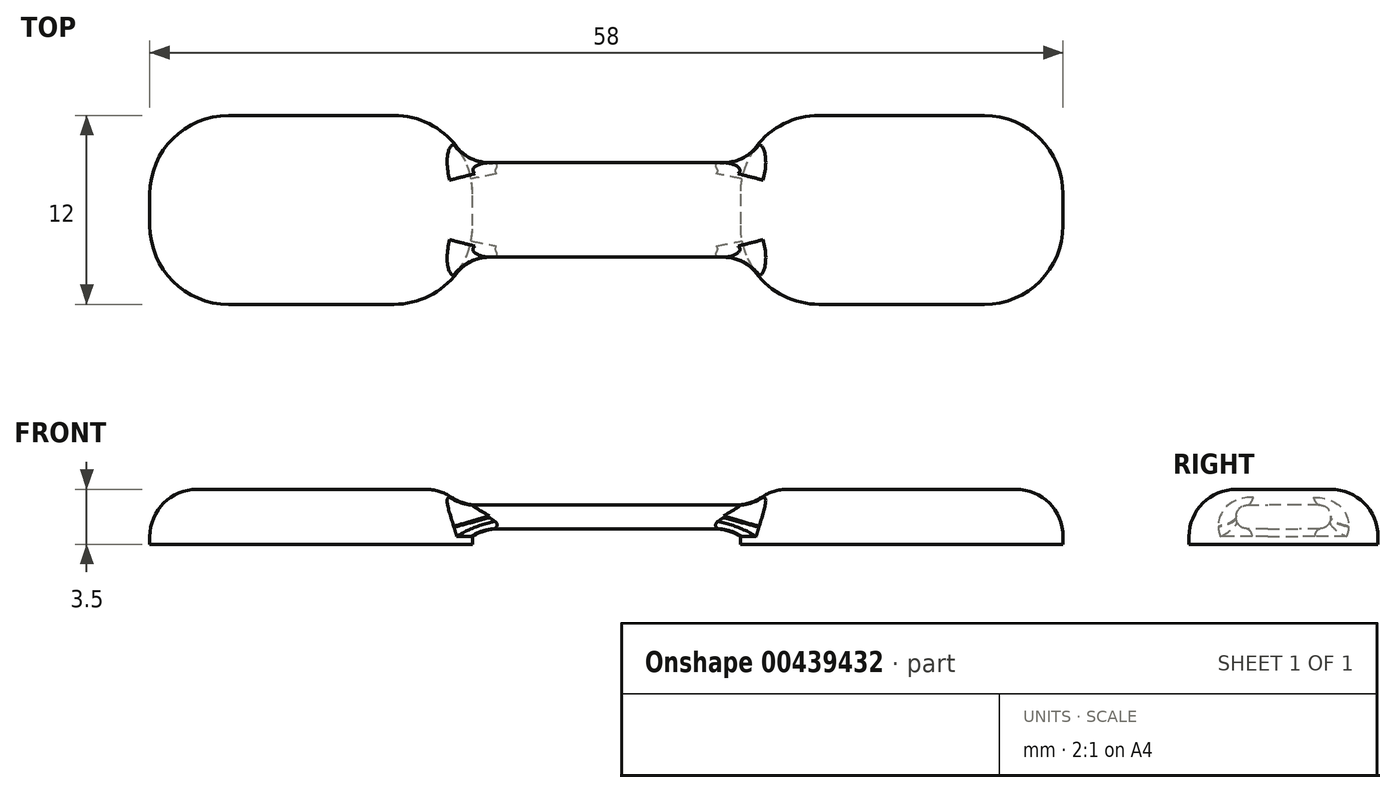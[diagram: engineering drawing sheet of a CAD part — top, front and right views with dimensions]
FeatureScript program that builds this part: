
annotation { "Feature Type Name" : "Feature", "Feature Type Description" : "" }
export const myFeature = defineFeature(function(context is Context, id is Id, definition is map)
    precondition{}
    {
        {
            var Q0;
            Q0=qCreatedBy(makeId("Top.planeOp"),FACE);
            var sketch = newSketch(context, id + "F0", { "sketchPlane" : qUnion([Q0])});
            skLineSegment(sketch, "E0.bottom", {"start": v(-29, 6) * mm, "end": v(29, 6) * mm});
            skLineSegment(sketch, "E0.top", {"start": v(-29, -6) * mm, "end": v(29, -6) * mm});
            skLineSegment(sketch, "E0.left", {"start": v(-29, 6) * mm, "end": v(-29, -6) * mm});
            skLineSegment(sketch, "E0.right", {"start": v(29, 6) * mm, "end": v(29, -6) * mm});
            skPoint(sketch, "E0.middle", {"position": v(0, 0) * mm});
            skSolve(sketch);
        }
        {
            var Q0;
            Q0=qSketchRegion(id+"F0",true);
            extrude(context, id + "F1", {"entities" : qUnion([Q0]), "depth" : 3.5 * mm});
        }
        {
            var Q0;
            Q0=qCreatedBy(makeId("Right.planeOp"),FACE);
            var sketch = newSketch(context, id + "F2", { "sketchPlane" : qUnion([Q0])});
            skLineSegment(sketch, "E1.bottom", {"start": v(3, 1) * mm, "end": v(-3, 1) * mm});
            skLineSegment(sketch, "E1.top", {"start": v(3, 2.5) * mm, "end": v(-3, 2.5) * mm});
            skLineSegment(sketch, "E1.left", {"start": v(3, 1) * mm, "end": v(3, 2.5) * mm});
            skLineSegment(sketch, "E1.right", {"start": v(-3, 1) * mm, "end": v(-3, 2.5) * mm});
            skPoint(sketch, "E1.middle", {"position": v(0, 1.75) * mm});
            skLineSegment(sketch, "E2", {"start": v(0, 1.75) * mm, "end": v(0, 0) * mm, "construction": true});
            skLineSegment(sketch, "E3.bottom", {"start": v(7, -0.75) * mm, "end": v(-7, -0.75) * mm});
            skLineSegment(sketch, "E3.top", {"start": v(7, 4.25) * mm, "end": v(-7, 4.25) * mm});
            skLineSegment(sketch, "E3.left", {"start": v(7, -0.75) * mm, "end": v(7, 4.25) * mm});
            skLineSegment(sketch, "E3.right", {"start": v(-7, -0.75) * mm, "end": v(-7, 4.25) * mm});
            skSolve(sketch);
        }
        {
            var Q0;
            Q0=qSketchRegion(id+"F2",true);
            extrude(context, id + "F3", {"entities" : qUnion([Q0]), "operationType" : NewBodyOperationType.REMOVE, "endBound" : BoundingType.SYMMETRIC, "oppositeDirection" : true, "depth" : 17 * mm});
        }
        {
            var Q0;
            Q0=makeQuery(id+"F1.opExtrude","SWEPT_EDGE",EDGE,{"disambiguationData":[OSD([sQuery(id+"F0.wireOp",EDGE,"E0.top"),sQuery(id+"F0.wireOp",EDGE,"E0.right")])]});
            var Q1;
            Q1=makeQuery(id+"F1.opExtrude","SWEPT_EDGE",EDGE,{"disambiguationData":[OSD([sQuery(id+"F0.wireOp",EDGE,"E0.bottom"),sQuery(id+"F0.wireOp",EDGE,"E0.right")])]});
            var Q2;
            Q2=makeQuery(id+"F1.opExtrude","SWEPT_EDGE",EDGE,{"disambiguationData":[OSD([sQuery(id+"F0.wireOp",EDGE,"E0.top"),sQuery(id+"F0.wireOp",EDGE,"E0.left")])]});
            var Q3;
            Q3=makeQuery(id+"F1.opExtrude","SWEPT_EDGE",EDGE,{"disambiguationData":[OSD([sQuery(id+"F0.wireOp",EDGE,"E0.bottom"),sQuery(id+"F0.wireOp",EDGE,"E0.left")])]});
            var Q4;
            Q4=makeQuery(id+"F3.boolean.opBoolean","INTERSECT",EDGE,{"derivedFrom":[makeQuery(id+"F1.opExtrude","SWEPT_FACE",FACE,{"disambiguationData":[OSD([sQuery(id+"F0.wireOp",EDGE,"E0.top")])]}),makeQuery(id+"F3.opExtrude","CAP_FACE",FACE,{"disambiguationData":[OSD([sQuery(id+"F2.wireOp",EDGE,"E1.bottom"),sQuery(id+"F2.wireOp",EDGE,"E1.top"),sQuery(id+"F2.wireOp",EDGE,"E1.left"),sQuery(id+"F2.wireOp",EDGE,"E1.right"),sQuery(id+"F2.wireOp",EDGE,"E3.bottom"),sQuery(id+"F2.wireOp",EDGE,"E3.top"),sQuery(id+"F2.wireOp",EDGE,"E3.left"),sQuery(id+"F2.wireOp",EDGE,"E3.right")])],"isStart":false})]});
            var Q5;
            Q5=makeQuery(id+"F3.boolean.opBoolean","INTERSECT",EDGE,{"derivedFrom":[makeQuery(id+"F1.opExtrude","SWEPT_FACE",FACE,{"disambiguationData":[OSD([sQuery(id+"F0.wireOp",EDGE,"E0.bottom")])]}),makeQuery(id+"F3.opExtrude","CAP_FACE",FACE,{"disambiguationData":[OSD([sQuery(id+"F2.wireOp",EDGE,"E1.bottom"),sQuery(id+"F2.wireOp",EDGE,"E1.top"),sQuery(id+"F2.wireOp",EDGE,"E1.left"),sQuery(id+"F2.wireOp",EDGE,"E1.right"),sQuery(id+"F2.wireOp",EDGE,"E3.bottom"),sQuery(id+"F2.wireOp",EDGE,"E3.top"),sQuery(id+"F2.wireOp",EDGE,"E3.left"),sQuery(id+"F2.wireOp",EDGE,"E3.right")])],"isStart":false})]});
            var Q6;
            Q6=makeQuery(id+"F3.boolean.opBoolean","INTERSECT",EDGE,{"derivedFrom":[makeQuery(id+"F1.opExtrude","SWEPT_FACE",FACE,{"disambiguationData":[OSD([sQuery(id+"F0.wireOp",EDGE,"E0.top")])]}),makeQuery(id+"F3.opExtrude","CAP_FACE",FACE,{"disambiguationData":[OSD([sQuery(id+"F2.wireOp",EDGE,"E1.bottom"),sQuery(id+"F2.wireOp",EDGE,"E1.top"),sQuery(id+"F2.wireOp",EDGE,"E1.left"),sQuery(id+"F2.wireOp",EDGE,"E1.right"),sQuery(id+"F2.wireOp",EDGE,"E3.bottom"),sQuery(id+"F2.wireOp",EDGE,"E3.top"),sQuery(id+"F2.wireOp",EDGE,"E3.left"),sQuery(id+"F2.wireOp",EDGE,"E3.right")])],"isStart":true})]});
            var Q7;
            Q7=makeQuery(id+"F3.boolean.opBoolean","INTERSECT",EDGE,{"derivedFrom":[makeQuery(id+"F1.opExtrude","SWEPT_FACE",FACE,{"disambiguationData":[OSD([sQuery(id+"F0.wireOp",EDGE,"E0.bottom")])]}),makeQuery(id+"F3.opExtrude","CAP_FACE",FACE,{"disambiguationData":[OSD([sQuery(id+"F2.wireOp",EDGE,"E1.bottom"),sQuery(id+"F2.wireOp",EDGE,"E1.top"),sQuery(id+"F2.wireOp",EDGE,"E1.left"),sQuery(id+"F2.wireOp",EDGE,"E1.right"),sQuery(id+"F2.wireOp",EDGE,"E3.bottom"),sQuery(id+"F2.wireOp",EDGE,"E3.top"),sQuery(id+"F2.wireOp",EDGE,"E3.left"),sQuery(id+"F2.wireOp",EDGE,"E3.right")])],"isStart":true})]});
            fillet(context, id + "F4", {"entities" : qUnion([Q0, Q1, Q2, Q3, Q4, Q5, Q6, Q7]), "radius" : 5 * mm, "tangentPropagation" : true, "allowEdgeOverflow" : false});
        }
        {
            var Q0;
            Q0=makeQuery(id+"F3.boolean.opBoolean","COPY",EDGE,{"derivedFrom":makeQuery(id+"F3.opExtrude","SWEPT_EDGE",EDGE,{"disambiguationData":[OSD([sQuery(id+"F2.wireOp",EDGE,"E1.top"),sQuery(id+"F2.wireOp",EDGE,"E1.left")])]})});
            var Q1;
            Q1=makeQuery(id+"F3.boolean.opBoolean","COPY",EDGE,{"derivedFrom":makeQuery(id+"F3.opExtrude","SWEPT_EDGE",EDGE,{"disambiguationData":[OSD([sQuery(id+"F2.wireOp",EDGE,"E1.top"),sQuery(id+"F2.wireOp",EDGE,"E1.right")])]})});
            var Q2;
            Q2=makeQuery(id+"F3.boolean.opBoolean","COPY",EDGE,{"derivedFrom":makeQuery(id+"F3.opExtrude","SWEPT_EDGE",EDGE,{"disambiguationData":[OSD([sQuery(id+"F2.wireOp",EDGE,"E1.bottom"),sQuery(id+"F2.wireOp",EDGE,"E1.right")])]})});
            var Q3;
            Q3=makeQuery(id+"F3.boolean.opBoolean","COPY",EDGE,{"derivedFrom":makeQuery(id+"F3.opExtrude","SWEPT_EDGE",EDGE,{"disambiguationData":[OSD([sQuery(id+"F2.wireOp",EDGE,"E1.bottom"),sQuery(id+"F2.wireOp",EDGE,"E1.left")])]})});
            fillet(context, id + "F5", {"entities" : qUnion([Q0, Q1, Q2, Q3]), "radius" : .7 * mm, "tangentPropagation" : true, "allowEdgeOverflow" : false});
        }
        {
            var Q0;
            {var subQ0=sQuery(id+"F0.wireOp",EDGE,"E0.bottom");var subQ1=makeQuery(id+"F3.opExtrude","CAP_FACE",FACE,{"disambiguationData":[OSD([sQuery(id+"F2.wireOp",EDGE,"E1.bottom"),sQuery(id+"F2.wireOp",EDGE,"E1.top"),sQuery(id+"F2.wireOp",EDGE,"E1.left"),sQuery(id+"F2.wireOp",EDGE,"E1.right"),sQuery(id+"F2.wireOp",EDGE,"E3.bottom"),sQuery(id+"F2.wireOp",EDGE,"E3.top"),sQuery(id+"F2.wireOp",EDGE,"E3.left"),sQuery(id+"F2.wireOp",EDGE,"E3.right")])],"isStart":false});var subQ2=sQuery(id+"F0.wireOp",EDGE,"E0.top");var subQ3=makeQuery(id+"F1.opExtrude","SWEPT_FACE",FACE,{"disambiguationData":[OSD([subQ2])]});var subQ4=sQuery(id+"F0.wireOp",EDGE,"E0.left");Q0=makeQuery(id+"F4.opFillet","BLEND_EDGE",EDGE,{"blendedFrom":[makeQuery(id+"F3.boolean.opBoolean","INTERSECT",EDGE,{"derivedFrom":[subQ3,subQ1]}),makeQuery(id+"F3.boolean.opBoolean","SPLIT",FACE,{"disambiguationData":[TD([makeQuery(id+"F1.opExtrude","SWEPT_FACE",FACE,{"disambiguationData":[OSD([subQ4])]})])],"derivedFrom":makeQuery(id+"F1.opExtrude","CAP_FACE",FACE,{"disambiguationData":[OSD([subQ0,subQ2,subQ4,sQuery(id+"F0.wireOp",EDGE,"E0.right")])],"isStart":false})})],"blendedInto":[makeQuery(id+"F3.boolean.opBoolean","SPLIT",FACE,{"disambiguationData":[TD([makeQuery(id+"F1.opExtrude","SWEPT_FACE",FACE,{"disambiguationData":[OSD([subQ4])]})])],"derivedFrom":makeQuery(id+"F1.opExtrude","CAP_FACE",FACE,{"disambiguationData":[OSD([subQ0,subQ2,subQ4,sQuery(id+"F0.wireOp",EDGE,"E0.right")])],"isStart":false})})]});}
            var Q1;
            {var subQ0=sQuery(id+"F0.wireOp",EDGE,"E0.bottom");var subQ1=sQuery(id+"F0.wireOp",EDGE,"E0.right");var subQ2=sQuery(id+"F0.wireOp",EDGE,"E0.top");var subQ3=makeQuery(id+"F1.opExtrude","SWEPT_FACE",FACE,{"disambiguationData":[OSD([subQ2])]});var subQ4=makeQuery(id+"F3.opExtrude","CAP_FACE",FACE,{"disambiguationData":[OSD([sQuery(id+"F2.wireOp",EDGE,"E1.bottom"),sQuery(id+"F2.wireOp",EDGE,"E1.top"),sQuery(id+"F2.wireOp",EDGE,"E1.left"),sQuery(id+"F2.wireOp",EDGE,"E1.right"),sQuery(id+"F2.wireOp",EDGE,"E3.bottom"),sQuery(id+"F2.wireOp",EDGE,"E3.top"),sQuery(id+"F2.wireOp",EDGE,"E3.left"),sQuery(id+"F2.wireOp",EDGE,"E3.right")])],"isStart":true});Q1=makeQuery(id+"F4.opFillet","BLEND_EDGE",EDGE,{"blendedFrom":[makeQuery(id+"F3.boolean.opBoolean","INTERSECT",EDGE,{"derivedFrom":[subQ3,subQ4]}),makeQuery(id+"F3.boolean.opBoolean","SPLIT",FACE,{"disambiguationData":[TD([makeQuery(id+"F1.opExtrude","SWEPT_FACE",FACE,{"disambiguationData":[OSD([subQ1])]})])],"derivedFrom":makeQuery(id+"F1.opExtrude","CAP_FACE",FACE,{"disambiguationData":[OSD([subQ0,subQ2,sQuery(id+"F0.wireOp",EDGE,"E0.left"),subQ1])],"isStart":false})})],"blendedInto":[makeQuery(id+"F3.boolean.opBoolean","SPLIT",FACE,{"disambiguationData":[TD([makeQuery(id+"F1.opExtrude","SWEPT_FACE",FACE,{"disambiguationData":[OSD([subQ1])]})])],"derivedFrom":makeQuery(id+"F1.opExtrude","CAP_FACE",FACE,{"disambiguationData":[OSD([subQ0,subQ2,sQuery(id+"F0.wireOp",EDGE,"E0.left"),subQ1])],"isStart":false})})]});}
            fillet(context, id + "F6", {"entities" : qUnion([Q0, Q1]), "radius" : 3 * mm, "tangentPropagation" : true, "allowEdgeOverflow" : false});
        }
        {
            var Q0;
            {var subQ0=sQuery(id+"F2.wireOp",EDGE,"E1.top");var subQ1=sQuery(id+"F0.wireOp",EDGE,"E0.bottom");var subQ2=makeQuery(id+"F1.opExtrude","SWEPT_FACE",FACE,{"disambiguationData":[OSD([subQ1])]});var subQ3=makeQuery(id+"F3.opExtrude","CAP_FACE",FACE,{"disambiguationData":[OSD([sQuery(id+"F2.wireOp",EDGE,"E1.bottom"),subQ0,sQuery(id+"F2.wireOp",EDGE,"E1.left"),sQuery(id+"F2.wireOp",EDGE,"E1.right"),sQuery(id+"F2.wireOp",EDGE,"E3.bottom"),sQuery(id+"F2.wireOp",EDGE,"E3.top"),sQuery(id+"F2.wireOp",EDGE,"E3.left"),sQuery(id+"F2.wireOp",EDGE,"E3.right")])],"isStart":false});var subQ4=sQuery(id+"F0.wireOp",EDGE,"E0.top");var subQ5=sQuery(id+"F0.wireOp",EDGE,"E0.left");Q0=makeQuery(id+"F6.opFillet","BLEND_EDGE",EDGE,{"disambiguationData":[OD(0.0)],"blendedFrom":[makeQuery(id+"F4.opFillet","BLEND_EDGE",EDGE,{"blendedFrom":[makeQuery(id+"F3.boolean.opBoolean","INTERSECT",EDGE,{"derivedFrom":[subQ2,subQ3]}),makeQuery(id+"F3.boolean.opBoolean","SPLIT",FACE,{"disambiguationData":[TD([makeQuery(id+"F1.opExtrude","SWEPT_FACE",FACE,{"disambiguationData":[OSD([subQ5])]})])],"derivedFrom":makeQuery(id+"F1.opExtrude","CAP_FACE",FACE,{"disambiguationData":[OSD([subQ1,subQ4,subQ5,sQuery(id+"F0.wireOp",EDGE,"E0.right")])],"isStart":false})})],"blendedInto":[makeQuery(id+"F3.boolean.opBoolean","SPLIT",FACE,{"disambiguationData":[TD([makeQuery(id+"F1.opExtrude","SWEPT_FACE",FACE,{"disambiguationData":[OSD([subQ5])]})])],"derivedFrom":makeQuery(id+"F1.opExtrude","CAP_FACE",FACE,{"disambiguationData":[OSD([subQ1,subQ4,subQ5,sQuery(id+"F0.wireOp",EDGE,"E0.right")])],"isStart":false})})]}),makeQuery(id+"F3.boolean.opBoolean","COPY",FACE,{"derivedFrom":makeQuery(id+"F3.opExtrude","SWEPT_FACE",FACE,{"disambiguationData":[OSD([subQ0])]})})],"blendedInto":[makeQuery(id+"F3.boolean.opBoolean","COPY",FACE,{"derivedFrom":makeQuery(id+"F3.opExtrude","SWEPT_FACE",FACE,{"disambiguationData":[OSD([subQ0])]})})]});}
            var Q1;
            {var subQ0=sQuery(id+"F2.wireOp",EDGE,"E1.top");var subQ1=sQuery(id+"F0.wireOp",EDGE,"E0.bottom");var subQ2=sQuery(id+"F0.wireOp",EDGE,"E0.right");var subQ3=sQuery(id+"F0.wireOp",EDGE,"E0.top");var subQ4=makeQuery(id+"F1.opExtrude","SWEPT_FACE",FACE,{"disambiguationData":[OSD([subQ3])]});var subQ5=makeQuery(id+"F3.opExtrude","CAP_FACE",FACE,{"disambiguationData":[OSD([sQuery(id+"F2.wireOp",EDGE,"E1.bottom"),subQ0,sQuery(id+"F2.wireOp",EDGE,"E1.left"),sQuery(id+"F2.wireOp",EDGE,"E1.right"),sQuery(id+"F2.wireOp",EDGE,"E3.bottom"),sQuery(id+"F2.wireOp",EDGE,"E3.top"),sQuery(id+"F2.wireOp",EDGE,"E3.left"),sQuery(id+"F2.wireOp",EDGE,"E3.right")])],"isStart":true});Q1=makeQuery(id+"F6.opFillet","BLEND_EDGE",EDGE,{"disambiguationData":[OD(0.0)],"blendedFrom":[makeQuery(id+"F4.opFillet","BLEND_EDGE",EDGE,{"blendedFrom":[makeQuery(id+"F3.boolean.opBoolean","INTERSECT",EDGE,{"derivedFrom":[subQ4,subQ5]}),makeQuery(id+"F3.boolean.opBoolean","SPLIT",FACE,{"disambiguationData":[TD([makeQuery(id+"F1.opExtrude","SWEPT_FACE",FACE,{"disambiguationData":[OSD([subQ2])]})])],"derivedFrom":makeQuery(id+"F1.opExtrude","CAP_FACE",FACE,{"disambiguationData":[OSD([subQ1,subQ3,sQuery(id+"F0.wireOp",EDGE,"E0.left"),subQ2])],"isStart":false})})],"blendedInto":[makeQuery(id+"F3.boolean.opBoolean","SPLIT",FACE,{"disambiguationData":[TD([makeQuery(id+"F1.opExtrude","SWEPT_FACE",FACE,{"disambiguationData":[OSD([subQ2])]})])],"derivedFrom":makeQuery(id+"F1.opExtrude","CAP_FACE",FACE,{"disambiguationData":[OSD([subQ1,subQ3,sQuery(id+"F0.wireOp",EDGE,"E0.left"),subQ2])],"isStart":false})})]}),makeQuery(id+"F3.boolean.opBoolean","COPY",FACE,{"derivedFrom":makeQuery(id+"F3.opExtrude","SWEPT_FACE",FACE,{"disambiguationData":[OSD([subQ0])]})})],"blendedInto":[makeQuery(id+"F3.boolean.opBoolean","COPY",FACE,{"derivedFrom":makeQuery(id+"F3.opExtrude","SWEPT_FACE",FACE,{"disambiguationData":[OSD([subQ0])]})})]});}
            fillet(context, id + "F7", {"entities" : qUnion([Q0, Q1]), "radius" : 3 * mm, "tangentPropagation" : true, "allowEdgeOverflow" : false});
        }
    });
